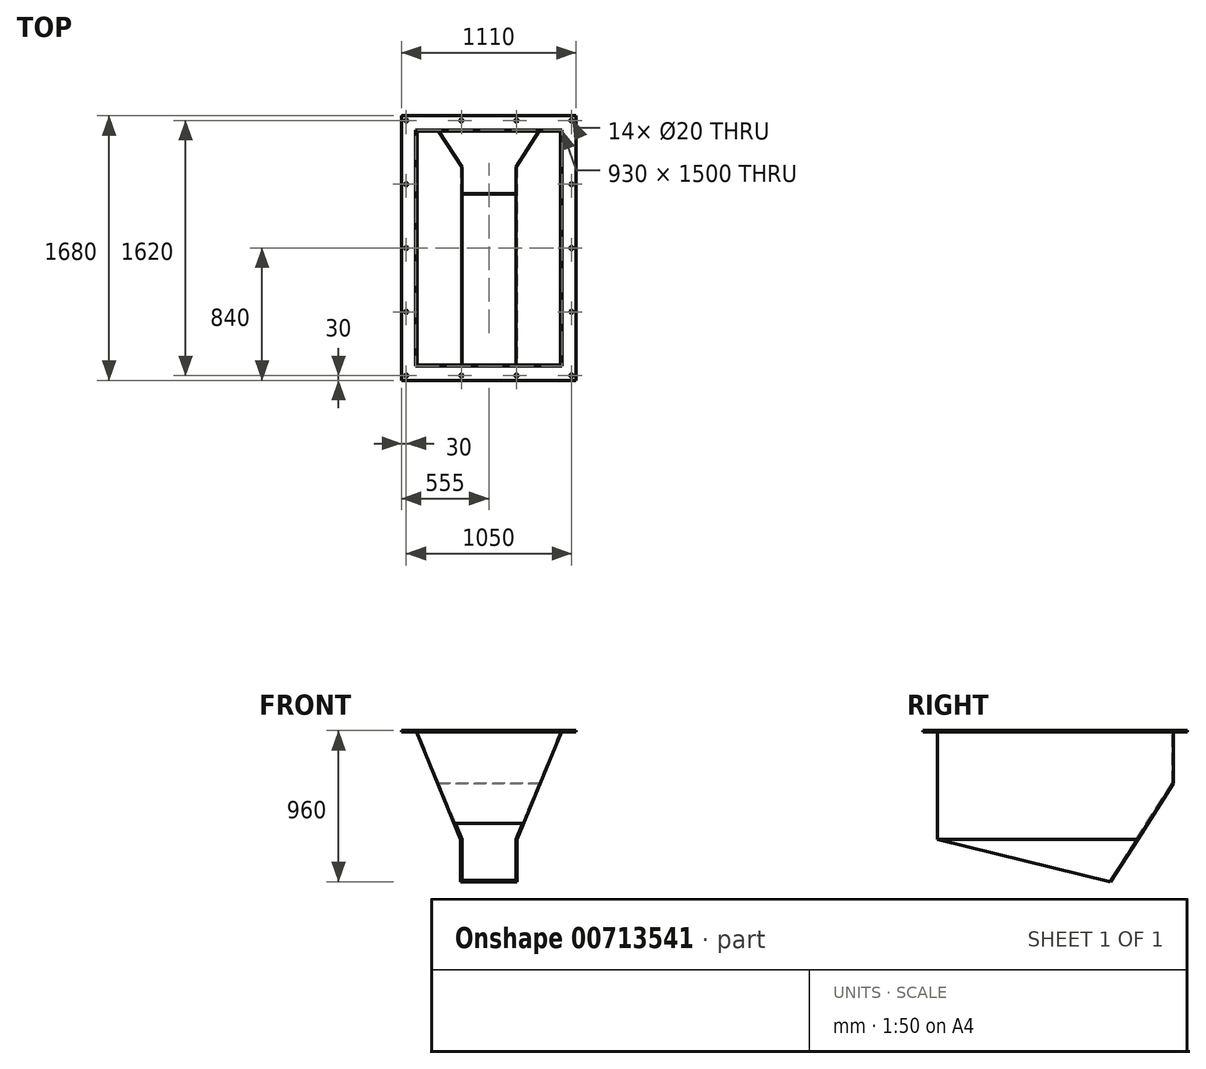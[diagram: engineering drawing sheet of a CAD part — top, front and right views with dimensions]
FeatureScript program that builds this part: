
annotation { "Feature Type Name" : "Feature", "Feature Type Description" : "" }
export const myFeature = defineFeature(function(context is Context, id is Id, definition is map)
    precondition{}
    {
        {
            var Q0;
            Q0=qCreatedBy(makeId("Front.planeOp"),FACE);
            var sketch = newSketch(context, id + "F0", { "sketchPlane" : qUnion([Q0])});
            skLineSegment(sketch, "E0", {"start": v(-465, 560) * mm, "end": v(465, 560) * mm});
            skLineSegment(sketch, "E1", {"start": v(465, 560) * mm, "end": v(180, -130) * mm});
            skLineSegment(sketch, "E2", {"start": v(-180, -130) * mm, "end": v(-465, 560) * mm});
            skLineSegment(sketch, "E3", {"start": v(-180, -130) * mm, "end": v(-180, -400) * mm});
            skLineSegment(sketch, "E4", {"start": v(-180, -400) * mm, "end": v(180, -400) * mm});
            skLineSegment(sketch, "E5", {"start": v(180, -400) * mm, "end": v(180, -130) * mm});
            skSolve(sketch);
        }
        {
            var Q0;
            Q0=qSketchRegion(id+"F0",true);
            extrude(context, id + "F1", {"entities" : qUnion([Q0]), "oppositeDirection" : true, "depth" : 1500 * mm, "offsetDistance" : 25 * mm});
        }
        {
            var Q0;
            Q0=makeQuery(id+"F1.opExtrude","SWEPT_FACE",FACE,{"disambiguationData":[OSD([sQuery(id+"F0.wireOp",EDGE,"E0")])]});
            var sketch = newSketch(context, id + "F2", { "sketchPlane" : qUnion([Q0])});
            skLineSegment(sketch, "E6", {"start": v(-465, 0) * mm, "end": v(-465, 1500) * mm});
            skLineSegment(sketch, "E7", {"start": v(-465, 1500) * mm, "end": v(465, 1500) * mm});
            skLineSegment(sketch, "E8", {"start": v(465, 1500) * mm, "end": v(465, 0) * mm});
            skLineSegment(sketch, "E9", {"start": v(465, 0) * mm, "end": v(-465, 0) * mm});
            skLineSegment(sketch, "E10.bottom", {"start": v(-555, -90) * mm, "end": v(555, -90) * mm});
            skLineSegment(sketch, "E10.top", {"start": v(-555, 1590) * mm, "end": v(555, 1590) * mm});
            skLineSegment(sketch, "E10.left", {"start": v(-555, -90) * mm, "end": v(-555, 1590) * mm});
            skLineSegment(sketch, "E10.right", {"start": v(555, -90) * mm, "end": v(555, 1590) * mm});
            skSolve(sketch);
        }
        {
            var Q0;
            Q0=qSketchRegion(id+"F2",true);
            extrude(context, id + "F3", {"entities" : qUnion([Q0]), "oppositeDirection" : true, "depth" : 10 * mm, "offsetDistance" : 25 * mm});
        }
        {
            var Q0;
            Q0=makeQuery(id+"F3.opExtrude","CAP_FACE",FACE,{"disambiguationData":[OSD([sQuery(id+"F2.wireOp",EDGE,"E6"),sQuery(id+"F2.wireOp",EDGE,"E7"),sQuery(id+"F2.wireOp",EDGE,"E8"),sQuery(id+"F2.wireOp",EDGE,"E9"),sQuery(id+"F2.wireOp",EDGE,"E10.bottom"),sQuery(id+"F2.wireOp",EDGE,"E10.top"),sQuery(id+"F2.wireOp",EDGE,"E10.left"),sQuery(id+"F2.wireOp",EDGE,"E10.right")])],"isStart":true});
            var sketch = newSketch(context, id + "F4", { "sketchPlane" : qUnion([Q0])});
            skCircle(sketch, "E11", {"center": v(-525, 1560) * mm, "radius": 10 * mm});
            skCircle(sketch, "E12", {"center": v(-175, 1560) * mm, "radius": 10 * mm});
            skCircle(sketch, "E13", {"center": v(175, 1560) * mm, "radius": 10 * mm});
            skCircle(sketch, "E14", {"center": v(525, 1560) * mm, "radius": 10 * mm});
            skLineSegment(sketch, "E15", {"start": v(-770.34, 750) * mm, "end": v(1029.88, 750) * mm, "construction": true});
            skPoint(sketch, "E15.startSnap0", {"position": v(-555, 750) * mm});
            skLineSegment(sketch, "E16", {"start": v(0, 1815.12) * mm, "end": v(0, -396.85) * mm, "construction": true});
            skPoint(sketch, "E16.startSnap0", {"position": v(0, 1590) * mm});
            skCircle(sketch, "E17", {"center": v(525, 1155) * mm, "radius": 10 * mm});
            skCircle(sketch, "E18", {"center": v(525, 750) * mm, "radius": 10 * mm});
            skCircle(sketch, "E19", {"center": v(525, 345) * mm, "radius": 10 * mm});
            skCircle(sketch, "E20", {"center": v(525, -60) * mm, "radius": 10 * mm});
            skCircle(sketch, "E21.MirrorC", {"center": v(-525, 1155) * mm, "radius": 10 * mm});
            skCircle(sketch, "E22.MirrorC", {"center": v(-525, 750) * mm, "radius": 10 * mm});
            skCircle(sketch, "E23.MirrorC", {"center": v(-525, 345) * mm, "radius": 10 * mm});
            skCircle(sketch, "E24.MirrorC", {"center": v(-525, -60) * mm, "radius": 10 * mm});
            skCircle(sketch, "E25.MirrorC", {"center": v(175, -60) * mm, "radius": 10 * mm});
            skCircle(sketch, "E26.MirrorC", {"center": v(-175, -60) * mm, "radius": 10 * mm});
            skSolve(sketch);
        }
        {
            var Q0;
            Q0=qSketchRegion(id+"F4",true);
            extrude(context, id + "F5", {"entities" : qUnion([Q0]), "operationType" : NewBodyOperationType.REMOVE, "oppositeDirection" : true, "depth" : 10 * mm, "offsetDistance" : 25 * mm});
        }
        {
            var Q0;
            Q0=makeQuery(id+"F3.opExtrude","SWEPT_FACE",FACE,{"disambiguationData":[OSD([sQuery(id+"F2.wireOp",EDGE,"E10.right")])]});
            var sketch = newSketch(context, id + "F6", { "sketchPlane" : qUnion([Q0])});
            skLineSegment(sketch, "E27", {"start": v(750, 560) * mm, "end": v(1500, 560) * mm, "construction": true});
            skLineSegment(sketch, "E28", {"start": v(1500, 560) * mm, "end": v(1500, 225) * mm, "construction": true});
            skLineSegment(sketch, "E29", {"start": v(1500, 225) * mm, "end": v(1100, 225) * mm, "construction": true});
            skLineSegment(sketch, "E30", {"start": v(1100, 225) * mm, "end": v(1100, -400) * mm, "construction": true});
            skLineSegment(sketch, "E31", {"start": v(1100, -400) * mm, "end": v(1500, 225) * mm});
            skLineSegment(sketch, "E32", {"start": v(1500, 225) * mm, "end": v(1500, -400) * mm});
            skLineSegment(sketch, "E33", {"start": v(0, -130) * mm, "end": v(1100, -400) * mm});
            skLineSegment(sketch, "E34", {"start": v(0, -400) * mm, "end": v(0, -130) * mm});
            skLineSegment(sketch, "E35", {"start": v(0, -400) * mm, "end": v(1500, -400) * mm});
            skSolve(sketch);
        }
        {
            var Q0;
            Q0 = qSketchRegion(id + "F6", true);
            extrude(context, id + "F7", {"entities" : qUnion([Q0]), "operationType" : NewBodyOperationType.REMOVE, "endBound" : BoundingType.THROUGH_ALL, "oppositeDirection" : true, "depth" : 25 * mm, "offsetDistance" : 25 * mm});
        }
        {
            var Q0;
            Q0=makeQuery(id+"F1.opExtrude","SWEPT_FACE",FACE,{"disambiguationData":[OSD([sQuery(id+"F0.wireOp",EDGE,"E0")])]});
            shell(context, id + "F8", {"entities" : qUnion([Q0]), "thickness" : 8 * mm});
        }
        {
            var Q0;
            Q0=qCreatedBy(makeId("Front.planeOp"),FACE);
            var sketch = newSketch(context, id + "F9", { "sketchPlane" : qUnion([Q0])});
            skLineSegment(sketch, "E36", {"start": v(0, 0) * mm, "end": v(0, -130) * mm, "construction": true});
            skLineSegment(sketch, "E37", {"start": v(0, 0) * mm, "end": v(0, 560) * mm, "construction": true});
            skLineSegment(sketch, "E38", {"start": v(0, 560) * mm, "end": v(-465, 560) * mm, "construction": true});
            skLineSegment(sketch, "E39", {"start": v(-212.65, -30) * mm, "end": v(212.65, -30) * mm});
            skLineSegment(sketch, "E40", {"start": v(212.65, -30) * mm, "end": v(171.34, -130) * mm});
            skLineSegment(sketch, "E41", {"start": v(-171.34, -130) * mm, "end": v(-212.65, -30) * mm});
            skLineSegment(sketch, "E42", {"start": v(171.34, -130) * mm, "end": v(-171.34, -130) * mm});
            skSolve(sketch);
        }
        {
            var Q0;
            Q0=qSketchRegion(id+"F9",true);
            extrude(context, id + "F10", {"entities" : qUnion([Q0]), "operationType" : NewBodyOperationType.REMOVE, "oppositeDirection" : true, "depth" : 8 * mm, "offsetDistance" : 25 * mm});
        }
        {
            var Q0;
            Q0=makeQuery(id+"F7.boolean.opBoolean","COPY",FACE,{"derivedFrom":makeQuery(id+"F7.opExtrude","SWEPT_FACE",FACE,{"disambiguationData":[OSD([sQuery(id+"F6.wireOp",EDGE,"E33")])]})});
            var sketch = newSketch(context, id + "F11", { "sketchPlane" : qUnion([Q0])});
            skLineSegment(sketch, "E43.bottom", {"start": v(172, -30.99) * mm, "end": v(-172, -30.99) * mm});
            skLineSegment(sketch, "E43.top", {"start": v(172, -1155.64) * mm, "end": v(-172, -1155.64) * mm});
            skLineSegment(sketch, "E43.left", {"start": v(172, -30.99) * mm, "end": v(172, -1155.64) * mm});
            skLineSegment(sketch, "E43.right", {"start": v(-172, -30.99) * mm, "end": v(-172, -1155.64) * mm});
            skSolve(sketch);
        }
        {
            var Q0;
            Q0 = qSketchRegion(id + "F11", true);
            extrude(context, id + "F12", {"entities" : qUnion([Q0]), "operationType" : NewBodyOperationType.REMOVE, "oppositeDirection" : true, "depth" : 8 * mm, "offsetDistance" : 25 * mm});
        }
    });
